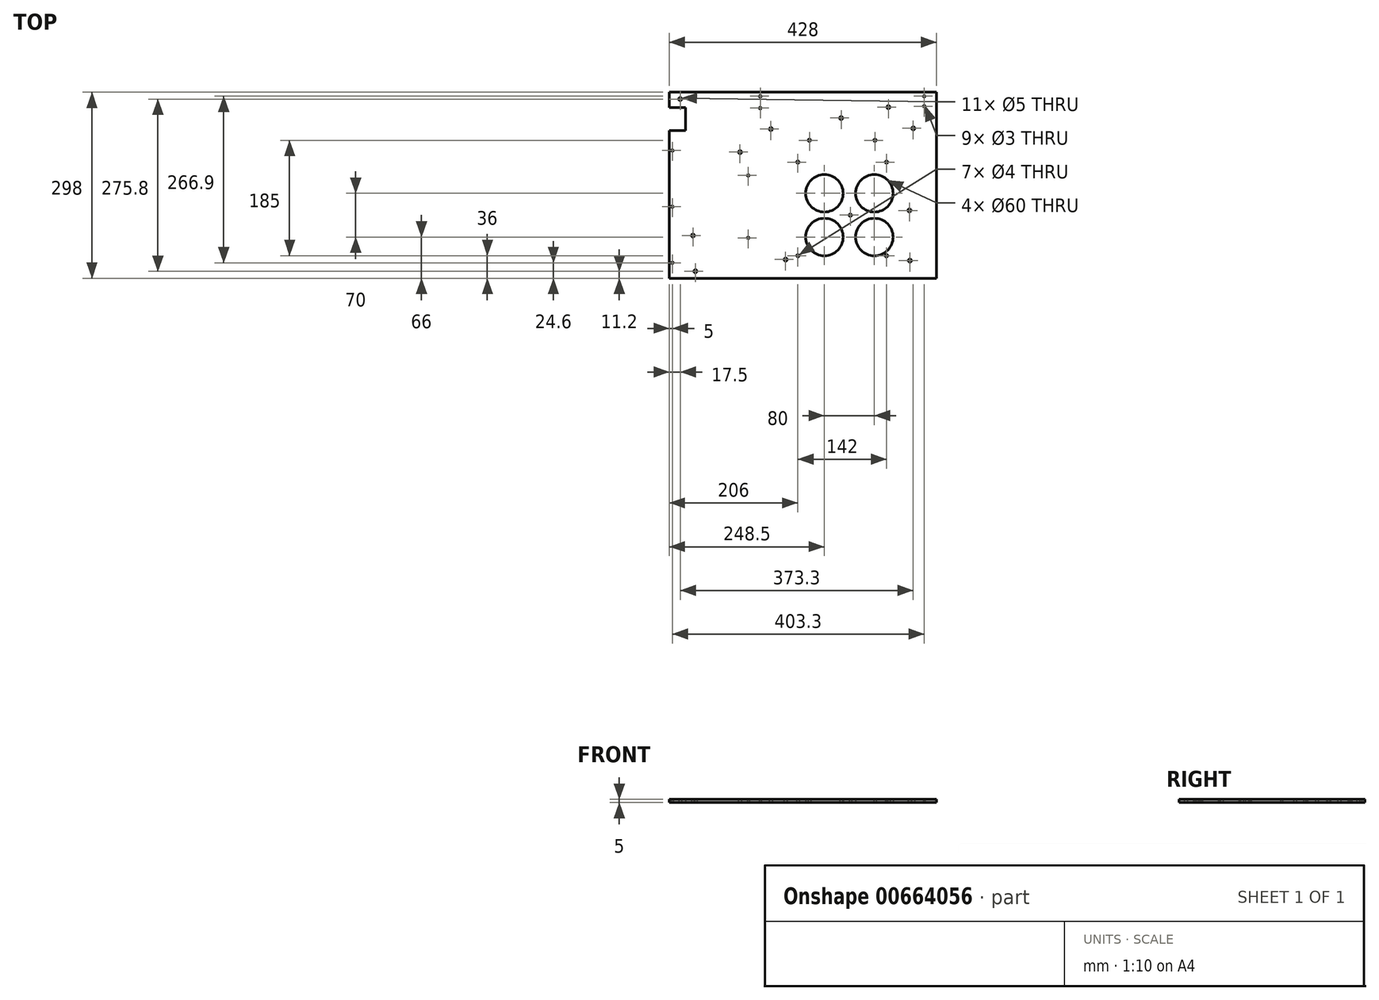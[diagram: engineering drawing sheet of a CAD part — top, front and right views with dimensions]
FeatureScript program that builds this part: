
annotation { "Feature Type Name" : "Feature", "Feature Type Description" : "" }
export const myFeature = defineFeature(function(context is Context, id is Id, definition is map)
    precondition{}
    {
        {
            var Q0;
            Q0=qCreatedBy(makeId("Top.planeOp"),FACE);
            var sketch = newSketch(context, id + "F0", { "sketchPlane" : qUnion([Q0])});
            skLineSegment(sketch, "E0.bottom", {"start": v(0, 298) * mm, "end": v(428, 298) * mm});
            skLineSegment(sketch, "E0.top", {"start": v(0, 0) * mm, "end": v(428, 0) * mm});
            skLineSegment(sketch, "E0.left", {"start": v(0, 298) * mm, "end": v(0, 0) * mm});
            skLineSegment(sketch, "E0.right", {"start": v(428, 298) * mm, "end": v(428, 0) * mm});
            skCircle(sketch, "E1", {"center": v(328.5, 66) * mm, "radius": 30 * mm});
            skCircle(sketch, "E2", {"center": v(328.5, 136) * mm, "radius": 30 * mm});
            skCircle(sketch, "E3", {"center": v(248.5, 66) * mm, "radius": 30 * mm});
            skCircle(sketch, "E4", {"center": v(248.5, 136) * mm, "radius": 30 * mm});
            skCircle(sketch, "E5", {"center": v(5, 24.6) * mm, "radius": 1.5 * mm});
            skCircle(sketch, "E6", {"center": v(5, 114.6) * mm, "radius": 1.5 * mm});
            skCircle(sketch, "E7", {"center": v(5, 204.6) * mm, "radius": 1.5 * mm});
            skCircle(sketch, "E8", {"center": v(126.5, 64.6) * mm, "radius": 1.5 * mm});
            skCircle(sketch, "E9", {"center": v(126.5, 164.6) * mm, "radius": 1.5 * mm});
            skCircle(sketch, "E10", {"center": v(145.8, 272.5) * mm, "radius": 1.5 * mm});
            skCircle(sketch, "E11", {"center": v(145.8, 291.5) * mm, "radius": 1.5 * mm});
            skCircle(sketch, "E12", {"center": v(408.3, 275.5) * mm, "radius": 1.5 * mm});
            skCircle(sketch, "E13", {"center": v(408.3, 291.5) * mm, "radius": 1.5 * mm});
            skCircle(sketch, "E14", {"center": v(37.9, 68.4) * mm, "radius": 2.5 * mm});
            skCircle(sketch, "E15", {"center": v(41.8, 11.2) * mm, "radius": 2.5 * mm});
            skCircle(sketch, "E16", {"center": v(113.3, 202) * mm, "radius": 2.5 * mm});
            skCircle(sketch, "E17", {"center": v(162.8, 239) * mm, "radius": 2.5 * mm});
            skCircle(sketch, "E18", {"center": v(186.3, 29.9) * mm, "radius": 2.5 * mm});
            skCircle(sketch, "E19", {"center": v(275.3, 256.6) * mm, "radius": 2.5 * mm});
            skCircle(sketch, "E20", {"center": v(385.4, 28.2) * mm, "radius": 2.5 * mm});
            skCircle(sketch, "E21", {"center": v(384.8, 108.6) * mm, "radius": 2.5 * mm});
            skCircle(sketch, "E22", {"center": v(390.8, 240.1) * mm, "radius": 2.5 * mm});
            skCircle(sketch, "E23", {"center": v(206, 36) * mm, "radius": 2 * mm});
            skCircle(sketch, "E24", {"center": v(206, 186) * mm, "radius": 2 * mm});
            skCircle(sketch, "E25", {"center": v(224.5, 221) * mm, "radius": 2 * mm});
            skCircle(sketch, "E26", {"center": v(329.5, 221) * mm, "radius": 2 * mm});
            skCircle(sketch, "E27", {"center": v(290, 101) * mm, "radius": 2 * mm});
            skCircle(sketch, "E28", {"center": v(348, 186) * mm, "radius": 2 * mm});
            skCircle(sketch, "E29", {"center": v(348, 36) * mm, "radius": 2 * mm});
            skCircle(sketch, "E30", {"center": v(17.5, 287) * mm, "radius": 2.5 * mm});
            skCircle(sketch, "E31", {"center": v(351, 274) * mm, "radius": 2.5 * mm});
            skLineSegment(sketch, "E32.bottom", {"start": v(0, 273.5) * mm, "end": v(26, 273.5) * mm});
            skLineSegment(sketch, "E32.top", {"start": v(0, 236.5) * mm, "end": v(26, 236.5) * mm});
            skLineSegment(sketch, "E32.left", {"start": v(0, 273.5) * mm, "end": v(0, 236.5) * mm});
            skLineSegment(sketch, "E32.right", {"start": v(26, 273.5) * mm, "end": v(26, 236.5) * mm});
            skSolve(sketch);
        }
        {
            var Q0;
            {var subQ1=sQuery(id+"F0.wireOp",EDGE,"E0.bottom");Q0=makeQuery(id+"F0.imprint","IMPRINT",FACE,{"disambiguationData":[TD([[makeQuery(id+"F0.imprint","IMPRINT",EDGE,{"derivedFrom":subQ1}),-1.0]])]});}
            extrude(context, id + "F1", {"entities" : qUnion([Q0]), "depth" : 5 * mm, "offsetDistance" : 25 * mm});
        }
    });
